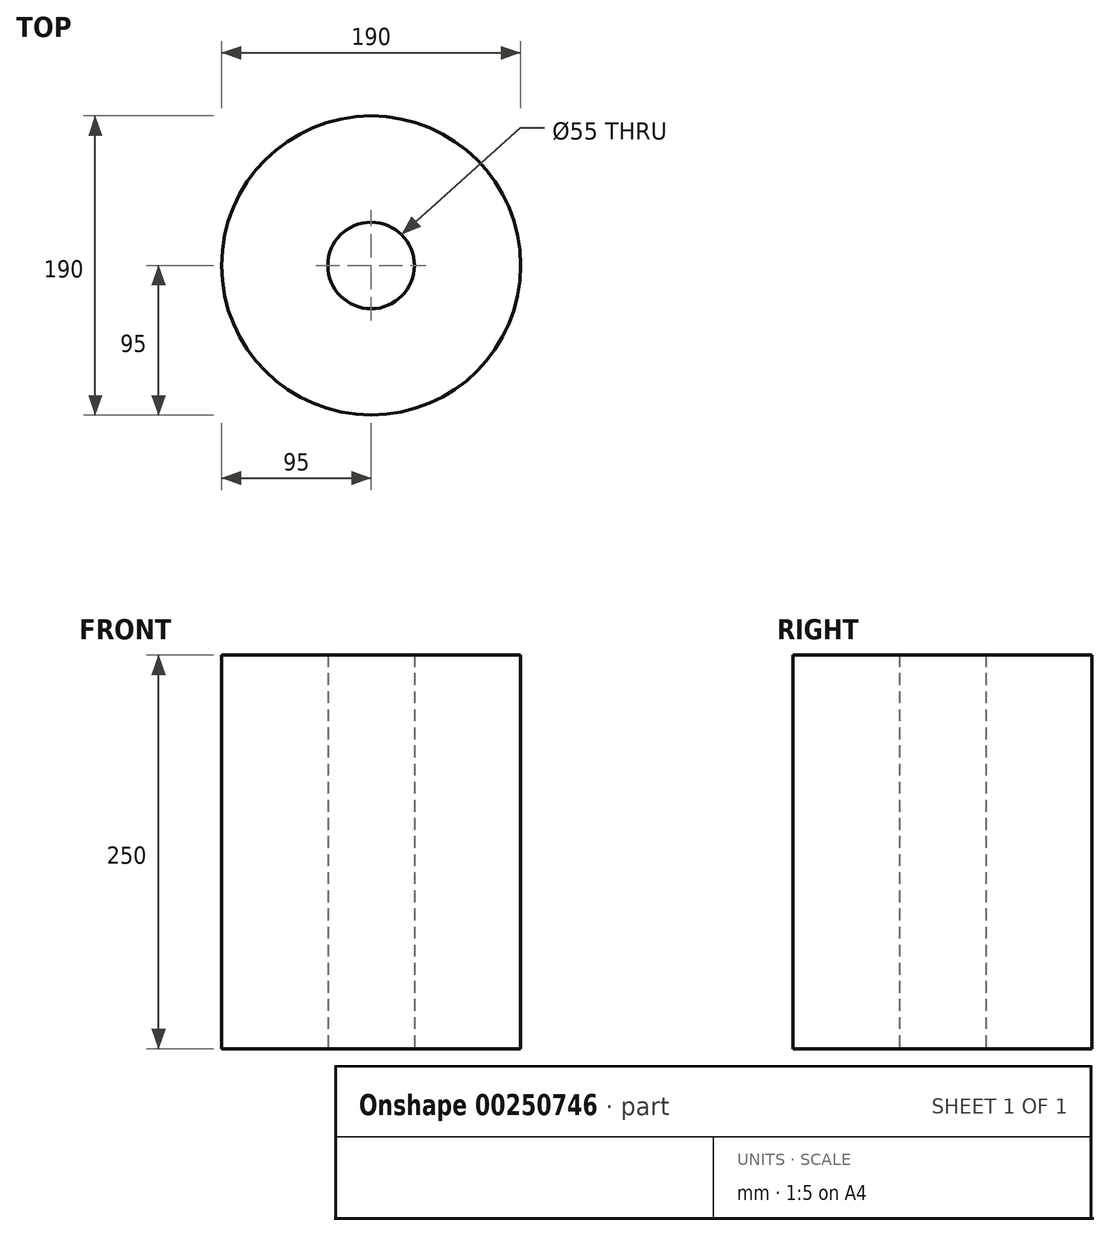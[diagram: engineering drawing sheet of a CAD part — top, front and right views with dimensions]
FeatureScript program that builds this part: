
annotation { "Feature Type Name" : "Feature", "Feature Type Description" : "" }
export const myFeature = defineFeature(function(context is Context, id is Id, definition is map)
    precondition{}
    {
        {
            var Q0;
            Q0=qCreatedBy(makeId("Top.planeOp"),FACE);
            var sketch = newSketch(context, id + "F0", { "sketchPlane" : qUnion([Q0])});
            skCircle(sketch, "E0", {"center": v(0, 0) * mm, "radius": 27.5 * mm});
            skCircle(sketch, "E1", {"center": v(0, 0) * mm, "radius": 95 * mm});
            skSolve(sketch);
        }
        {
            var Q0;
            Q0=makeQuery(id+"F0.imprint","IMPRINT",FACE,{"disambiguationData":[TD([[makeQuery(id+"F0.imprint","IMPRINT",EDGE,{"derivedFrom":sQuery(id+"F0.wireOp",EDGE,"E0")}),-1.0]])]});
            extrude(context, id + "F1", {"entities" : qUnion([Q0]), "depth" : 250 * mm});
        }
    });
